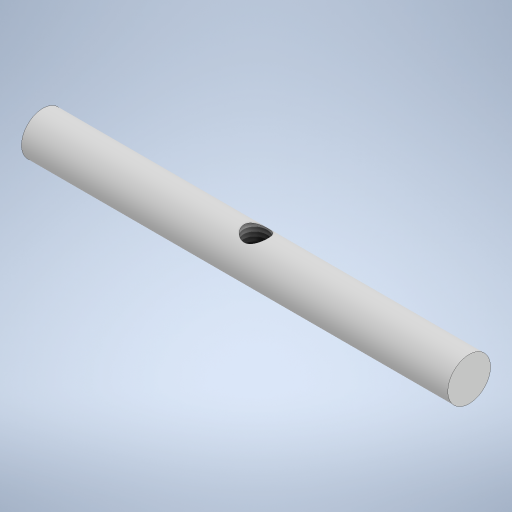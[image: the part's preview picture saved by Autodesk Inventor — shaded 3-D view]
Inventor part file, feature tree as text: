
AUTODESK INVENTOR PART (.ipt)
format: ipt  version: 2023 (Build 270158030, 158C)  size: 241,152 bytes
history: native  units: in
note: dims shown in document units (in); Inventor stores cm internally (conversion verified against a paired STEP export)
features: sketch x2, extrude x1, plane x1, hole x1
ambient origin geometry x8: Origin, YZ Plane, XZ Plane, XY Plane, X Axis, Y Axis, Z Axis, Center Point
bodies: Body1 (feature_tree)
feature tree (5):
  extrude  "Extrusion3"  Depth=5.9055in TaperAngle=0.0deg
  plane  "Work Plane1"
  hole  "Hole1"  [1 undecoded]
  sketch  "Sketch3"  dims[d6=0.5906in d7=5.9055in d8=0.0in]
  sketch  "Sketch6"  dims[d12=0.3298in d13=0.6299in d14=0.1575in d15=0.0787in d16=90.0deg d17=1.0748in d18=0.8108in]
note: 1 required parameter value undecoded (feature->parameter linkage not recoverable at this tier; creation-order binding heuristic only, values carry confidence <= 0.55)
